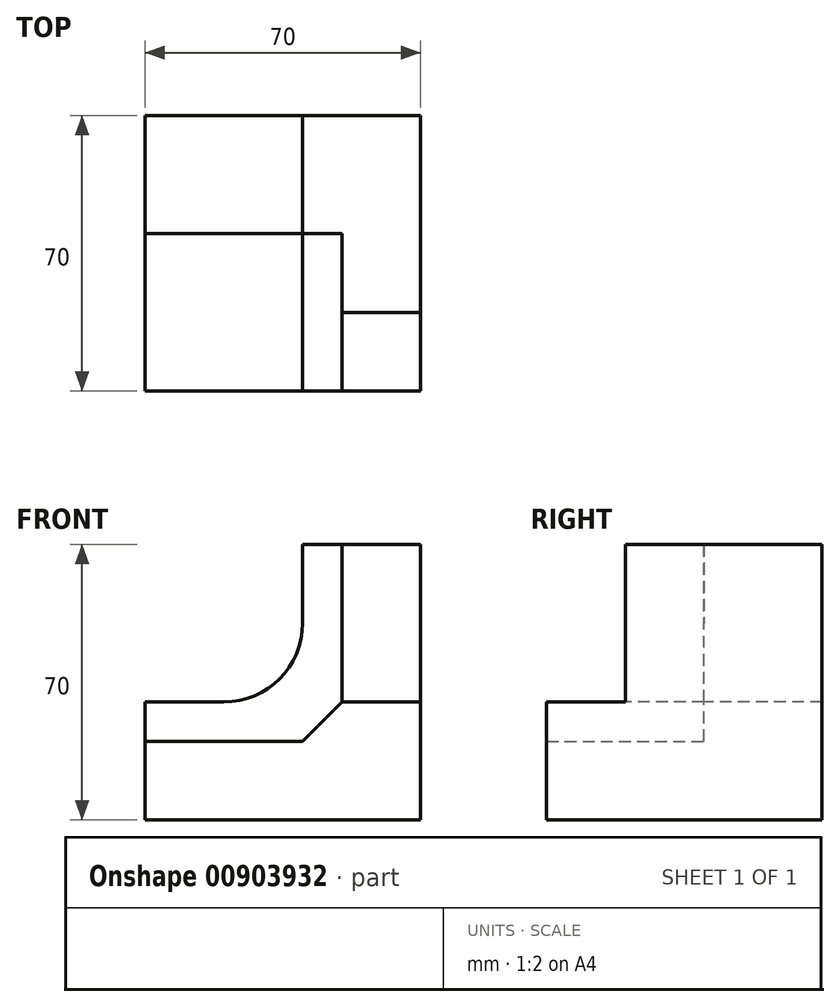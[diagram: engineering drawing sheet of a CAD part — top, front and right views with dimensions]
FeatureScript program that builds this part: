
annotation { "Feature Type Name" : "Feature", "Feature Type Description" : "" }
export const myFeature = defineFeature(function(context is Context, id is Id, definition is map)
    precondition{}
    {
        {
            var Q0;
            Q0=qCreatedBy(makeId("Top.planeOp"),FACE);
            var sketch = newSketch(context, id + "F0", { "sketchPlane" : qUnion([Q0])});
            skLineSegment(sketch, "E0.bottom", {"start": v(0, 0) * mm, "end": v(70, 0) * mm});
            skLineSegment(sketch, "E0.top", {"start": v(0, 70) * mm, "end": v(70, 70) * mm});
            skLineSegment(sketch, "E0.left", {"start": v(0, 0) * mm, "end": v(0, 70) * mm});
            skLineSegment(sketch, "E0.right", {"start": v(70, 0) * mm, "end": v(70, 70) * mm});
            skSolve(sketch);
        }
        {
            var Q0;
            Q0=makeQuery(id+"F0.imprint","IMPRINT",FACE,{"disambiguationData":[TD([[makeQuery(id+"F0.imprint","IMPRINT",EDGE,{"derivedFrom":sQuery(id+"F0.wireOp",EDGE,"E0.bottom")}),1.0]])]});
            extrude(context, id + "F1", {"entities" : qUnion([Q0]), "depth" : 70 * mm, "offsetDistance" : 25 * mm});
        }
        {
            var Q0;
            Q0=makeQuery(id+"F1.opExtrude","CAP_FACE",FACE,{"disambiguationData":[OSD([sQuery(id+"F0.wireOp",EDGE,"E0.bottom"),sQuery(id+"F0.wireOp",EDGE,"E0.top"),sQuery(id+"F0.wireOp",EDGE,"E0.left"),sQuery(id+"F0.wireOp",EDGE,"E0.right")])],"isStart":false});
            var sketch = newSketch(context, id + "F2", { "sketchPlane" : qUnion([Q0])});
            skLineSegment(sketch, "E1.bottom", {"start": v(0, 40) * mm, "end": v(50, 40) * mm});
            skLineSegment(sketch, "E1.top", {"start": v(0, 0) * mm, "end": v(50, 0) * mm});
            skLineSegment(sketch, "E1.left", {"start": v(0, 40) * mm, "end": v(0, 0) * mm});
            skLineSegment(sketch, "E1.right", {"start": v(50, 40) * mm, "end": v(50, 0) * mm});
            skSolve(sketch);
        }
        {
            var Q0;
            Q0=makeQuery(id+"F2.imprint","IMPRINT",FACE,{"disambiguationData":[TD([[makeQuery(id+"F2.imprint","IMPRINT",EDGE,{"derivedFrom":sQuery(id+"F2.wireOp",EDGE,"E1.bottom")}),-1.0]])]});
            extrude(context, id + "F3", {"entities" : qUnion([Q0]), "operationType" : NewBodyOperationType.REMOVE, "oppositeDirection" : true, "depth" : 50 * mm, "offsetDistance" : 25 * mm});
        }
        {
            var Q0;
            Q0=makeQuery(id+"F3.boolean.opBoolean","COPY",FACE,{"derivedFrom":makeQuery(id+"F3.opExtrude","SWEPT_FACE",FACE,{"disambiguationData":[OSD([sQuery(id+"F2.wireOp",EDGE,"E1.bottom")])]})});
            var sketch = newSketch(context, id + "F4", { "sketchPlane" : qUnion([Q0])});
            skLineSegment(sketch, "E2.bottom", {"start": v(0, 70) * mm, "end": v(40, 70) * mm});
            skLineSegment(sketch, "E2.top", {"start": v(0, 30) * mm, "end": v(40, 30) * mm});
            skLineSegment(sketch, "E2.left", {"start": v(0, 70) * mm, "end": v(0, 30) * mm});
            skLineSegment(sketch, "E2.right", {"start": v(40, 70) * mm, "end": v(40, 30) * mm});
            skSolve(sketch);
        }
        {
            var Q0;
            Q0=makeQuery(id+"F4.imprint","IMPRINT",FACE,{"disambiguationData":[TD([[makeQuery(id+"F4.imprint","IMPRINT",EDGE,{"derivedFrom":sQuery(id+"F4.wireOp",EDGE,"E2.bottom")}),-1.0]])]});
            extrude(context, id + "F5", {"entities" : qUnion([Q0]), "operationType" : NewBodyOperationType.REMOVE, "endBound" : BoundingType.THROUGH_ALL, "oppositeDirection" : true, "depth" : 25 * mm, "offsetDistance" : 25 * mm});
        }
        {
            var Q0;
            Q0=makeQuery(id+"F5.boolean.opBoolean","COPY",EDGE,{"derivedFrom":makeQuery(id+"F5.opExtrude","SWEPT_EDGE",EDGE,{"disambiguationData":[OSD([sQuery(id+"F4.wireOp",EDGE,"E2.top"),sQuery(id+"F4.wireOp",EDGE,"E2.right")])]})});
            fillet(context, id + "F6", {"entities" : qUnion([Q0]), "radius" : 20 * mm, "tangentPropagation" : true, "allowEdgeOverflow" : false});
        }
        {
            var Q0;
            Q0=makeQuery(id+"F3.boolean.opBoolean","COPY",FACE,{"derivedFrom":makeQuery(id+"F3.opExtrude","SWEPT_FACE",FACE,{"disambiguationData":[OSD([sQuery(id+"F2.wireOp",EDGE,"E1.right")])]})});
            var sketch = newSketch(context, id + "F7", { "sketchPlane" : qUnion([Q0])});
            skLineSegment(sketch, "E3.bottom", {"start": v(0, 70) * mm, "end": v(-20, 70) * mm});
            skLineSegment(sketch, "E3.top", {"start": v(0, 30) * mm, "end": v(-20, 30) * mm});
            skLineSegment(sketch, "E3.left", {"start": v(0, 70) * mm, "end": v(0, 30) * mm});
            skLineSegment(sketch, "E3.right", {"start": v(-20, 70) * mm, "end": v(-20, 30) * mm});
            skSolve(sketch);
        }
        {
            var Q0;
            Q0=makeQuery(id+"F7.imprint","IMPRINT",FACE,{"disambiguationData":[TD([[makeQuery(id+"F7.imprint","IMPRINT",EDGE,{"derivedFrom":sQuery(id+"F7.wireOp",EDGE,"E3.bottom")}),-1.0]])]});
            extrude(context, id + "F8", {"entities" : qUnion([Q0]), "operationType" : NewBodyOperationType.REMOVE, "endBound" : BoundingType.THROUGH_ALL, "oppositeDirection" : true, "depth" : 25 * mm, "offsetDistance" : 25 * mm});
        }
        {
            var Q0;
            Q0=makeQuery(id+"F3.boolean.opBoolean","COPY",EDGE,{"derivedFrom":makeQuery(id+"F3.opExtrude","CAP_EDGE",EDGE,{"disambiguationData":[OSD([sQuery(id+"F2.wireOp",EDGE,"E1.right")])],"isStart":false})});
            chamfer(context, id + "F9", {"entities" : qUnion([Q0]), "width" : 10 * mm, "tangentPropagation" : true});
        }
    });
